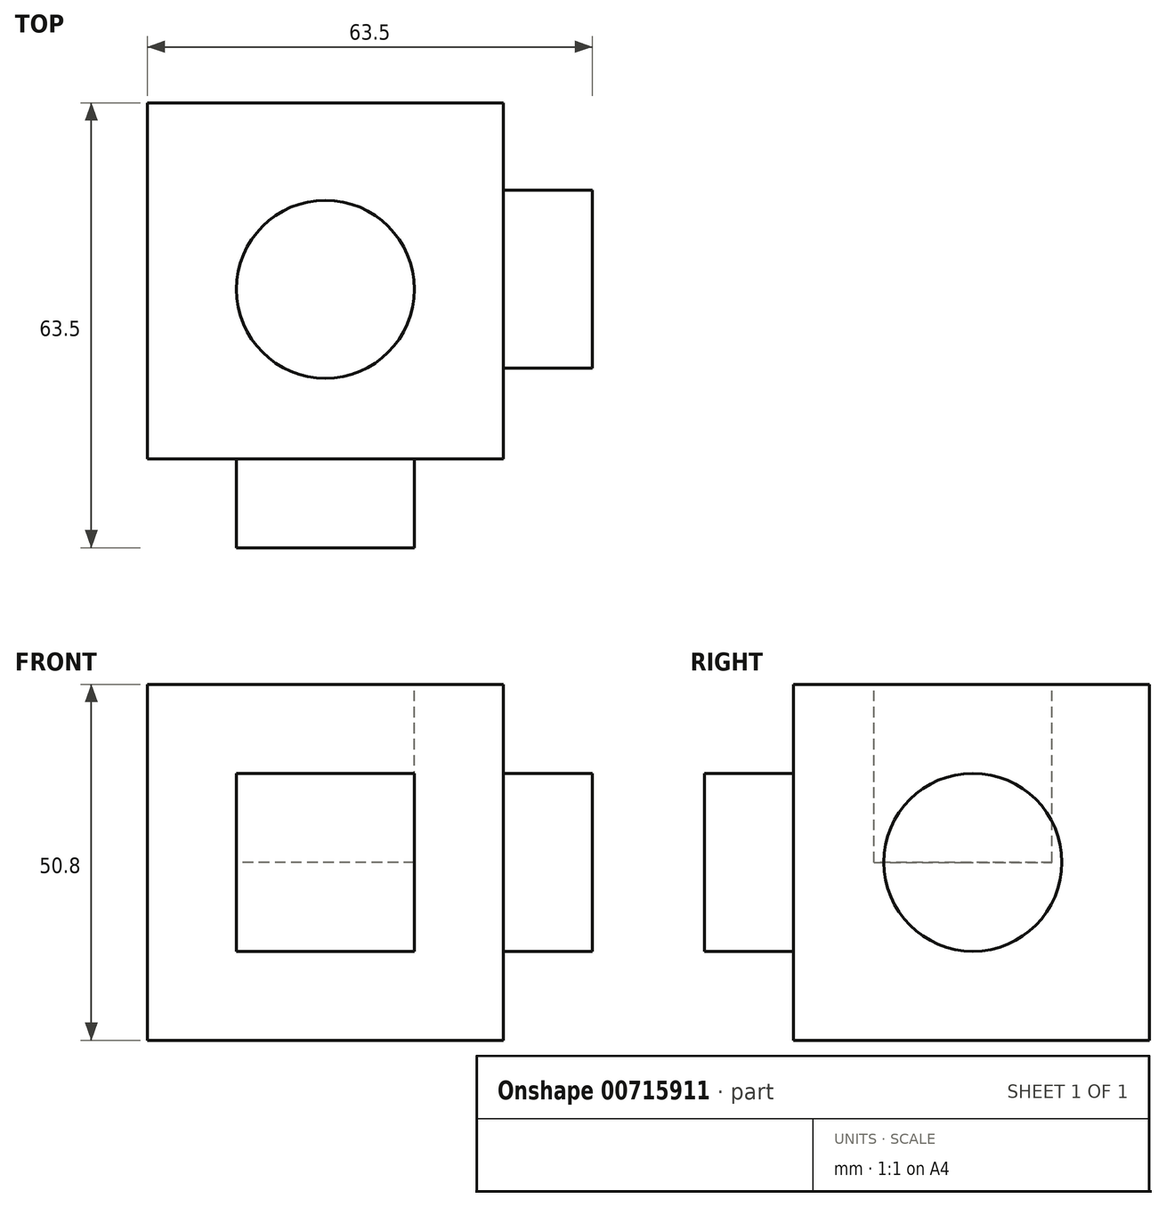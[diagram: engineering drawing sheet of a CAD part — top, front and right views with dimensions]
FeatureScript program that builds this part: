
annotation { "Feature Type Name" : "Feature", "Feature Type Description" : "" }
export const myFeature = defineFeature(function(context is Context, id is Id, definition is map)
    precondition{}
    {
        {
            var Q0;
            Q0=qCreatedBy(makeId("Front.planeOp"),FACE);
            var sketch = newSketch(context, id + "F0", { "sketchPlane" : qUnion([Q0])});
            skLineSegment(sketch, "E0.bottom", {"start": v(-25.4, 25.4) * mm, "end": v(25.4, 25.4) * mm});
            skLineSegment(sketch, "E0.top", {"start": v(-25.4, -25.4) * mm, "end": v(25.4, -25.4) * mm});
            skLineSegment(sketch, "E0.left", {"start": v(-25.4, 25.4) * mm, "end": v(-25.4, -25.4) * mm});
            skLineSegment(sketch, "E0.right", {"start": v(25.4, 25.4) * mm, "end": v(25.4, -25.4) * mm});
            skPoint(sketch, "E0.middle", {"position": v(0, 0) * mm});
            skSolve(sketch);
        }
        {
            var Q0;
            Q0 = qSketchRegion(id + "F0", true);
            extrude(context, id + "F1", {"entities" : qUnion([Q0]), "depth" : 50.8 * mm, "offsetDistance" : 25.4 * mm});
        }
        {
            var Q0;
            Q0=makeQuery(id+"F1.opExtrude","CAP_FACE",FACE,{"disambiguationData":[OSD([sQuery(id+"F0.wireOp",EDGE,"E0.bottom"),sQuery(id+"F0.wireOp",EDGE,"E0.top"),sQuery(id+"F0.wireOp",EDGE,"E0.left"),sQuery(id+"F0.wireOp",EDGE,"E0.right")])],"isStart":false});
            var sketch = newSketch(context, id + "F2", { "sketchPlane" : qUnion([Q0])});
            skLineSegment(sketch, "E1.bottom", {"start": v(-12.7, 12.7) * mm, "end": v(12.7, 12.7) * mm});
            skLineSegment(sketch, "E1.top", {"start": v(-12.7, -12.7) * mm, "end": v(12.7, -12.7) * mm});
            skLineSegment(sketch, "E1.left", {"start": v(-12.7, 12.7) * mm, "end": v(-12.7, -12.7) * mm});
            skLineSegment(sketch, "E1.right", {"start": v(12.7, 12.7) * mm, "end": v(12.7, -12.7) * mm});
            skPoint(sketch, "E1.middle", {"position": v(0, 0) * mm});
            skSolve(sketch);
        }
        {
            var Q0;
            Q0=makeQuery(id+"F2.imprint","IMPRINT",FACE,{"disambiguationData":[TD([[makeQuery(id+"F2.imprint","IMPRINT",EDGE,{"derivedFrom":sQuery(id+"F2.wireOp",EDGE,"E1.bottom")}),-1.0]])]});
            extrude(context, id + "F3", {"entities" : qUnion([Q0]), "operationType" : NewBodyOperationType.ADD, "depth" : 12.7 * mm, "offsetDistance" : 25.4 * mm});
        }
        {
            var Q0;
            Q0=makeQuery(id+"F1.opExtrude","SWEPT_FACE",FACE,{"disambiguationData":[OSD([sQuery(id+"F0.wireOp",EDGE,"E0.right")])]});
            var sketch = newSketch(context, id + "F4", { "sketchPlane" : qUnion([Q0])});
            skCircle(sketch, "E2", {"center": v(-25.2, 0) * mm, "radius": 12.7 * mm});
            skSolve(sketch);
        }
        {
            var Q0;
            Q0=makeQuery(id+"F4.imprint","IMPRINT",FACE,{"disambiguationData":[TD([[makeQuery(id+"F4.imprint","IMPRINT",EDGE,{"derivedFrom":sQuery(id+"F4.wireOp",EDGE,"E2")}),1.0]])]});
            extrude(context, id + "F5", {"entities" : qUnion([Q0]), "operationType" : NewBodyOperationType.ADD, "depth" : 12.7 * mm, "offsetDistance" : 25.4 * mm});
        }
        {
            var Q0;
            Q0=makeQuery(id+"F1.opExtrude","SWEPT_FACE",FACE,{"disambiguationData":[OSD([sQuery(id+"F0.wireOp",EDGE,"E0.bottom")])]});
            var sketch = newSketch(context, id + "F6", { "sketchPlane" : qUnion([Q0])});
            skCircle(sketch, "E3", {"center": v(0, -26.63) * mm, "radius": 12.7 * mm});
            skSolve(sketch);
        }
        {
            var Q0;
            Q0 = qSketchRegion(id + "F6", true);
            extrude(context, id + "F7", {"entities" : qUnion([Q0]), "operationType" : NewBodyOperationType.REMOVE, "oppositeDirection" : true, "depth" : 25.4 * mm, "offsetDistance" : 25.4 * mm});
        }
    });
